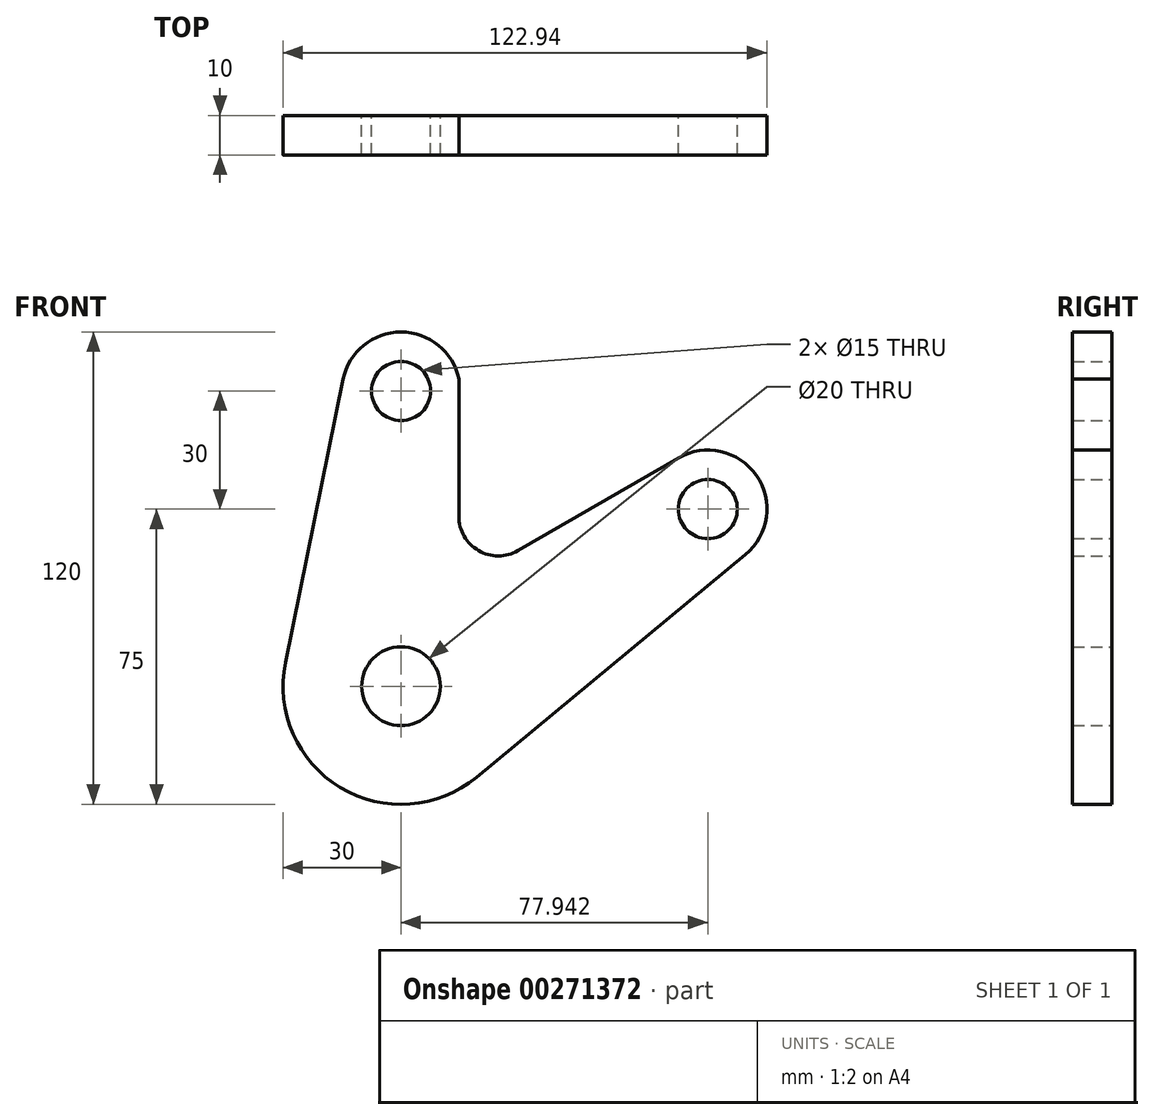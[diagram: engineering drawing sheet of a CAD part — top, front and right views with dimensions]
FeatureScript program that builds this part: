
annotation { "Feature Type Name" : "Feature", "Feature Type Description" : "" }
export const myFeature = defineFeature(function(context is Context, id is Id, definition is map)
    precondition{}
    {
        {
            var Q0;
            Q0=qCreatedBy(makeId("Front.planeOp"),FACE);
            var sketch = newSketch(context, id + "F0", { "sketchPlane" : qUnion([Q0])});
            skCircle(sketch, "E0", {"center": v(0, 0) * mm, "radius": 10 * mm});
            skCircle(sketch, "E1", {"center": v(0, 75) * mm, "radius": 7.5 * mm});
            skCircle(sketch, "E2", {"center": v(77.94, 45) * mm, "radius": 7.5 * mm});
            skArc(sketch, "E3", {"start": v(-29.4, 6) * mm, "mid": v(-15.44, -25.72) * mm, "end": v(19.12, -23.12) * mm});
            skLineSegment(sketch, "E4", {"start": v(-29.4, 6) * mm, "end": v(-14.7, 78) * mm});
            skArc(sketch, "E5", {"start": v(-14.7, 78) * mm, "mid": v(0, 90) * mm, "end": v(14.7, 78) * mm});
            skLineSegment(sketch, "E6", {"start": v(14.7, 78) * mm, "end": v(14.7, 43.13) * mm});
            skLineSegment(sketch, "E7", {"start": v(19.12, -23.12) * mm, "end": v(87.5, 33.44) * mm});
            skArc(sketch, "E8", {"start": v(14.7, 43.13) * mm, "mid": v(19.7, 34.47) * mm, "end": v(29.7, 34.47) * mm});
            skArc(sketch, "E9", {"start": v(87.5, 33.44) * mm, "mid": v(90.26, 53.56) * mm, "end": v(70.44, 58) * mm});
            skLineSegment(sketch, "E10", {"start": v(70.44, 58) * mm, "end": v(29.7, 34.47) * mm});
            skLineSegment(sketch, "E11", {"start": v(0, 0) * mm, "end": v(77.94, 45) * mm, "construction": true});
            skSolve(sketch);
        }
        {
            var Q0;
            Q0=makeQuery(id+"F0.imprint","IMPRINT",FACE,{"disambiguationData":[TD([[makeQuery(id+"F0.imprint","IMPRINT",EDGE,{"derivedFrom":sQuery(id+"F0.wireOp",EDGE,"E0")}),-1.0]])]});
            extrude(context, id + "F1", {"entities" : qUnion([Q0]), "depth" : 10 * mm});
        }
    });
